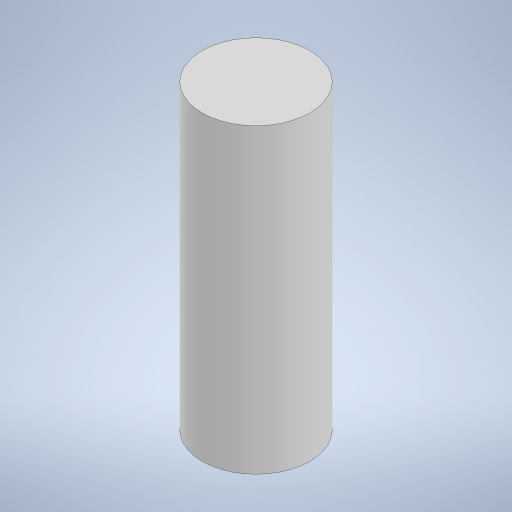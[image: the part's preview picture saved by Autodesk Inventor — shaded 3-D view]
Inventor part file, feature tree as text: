
AUTODESK INVENTOR PART (.ipt)
format: ipt  version: 2023 (Build 270158000, 158)  size: 206,336 bytes
history: native  units: mm
features: other x1, extrude x1, sketch x1
ambient origin geometry x8: Origin, YZ Plane, XZ Plane, XY Plane, X Axis, Y Axis, Z Axis, Center Point
bodies: Body1 (feature_tree)
feature tree (3):
  other  "Твердое тело1"
  extrude  "Выдавливание1"  Depth=10.0mm
  sketch  "Эскиз1"
